# Revit family: Lighting_Outside_Focus-Lighting_Nyx-330_Lantern
name_source: partatom
category: Lighting Fixtures
revit_build: Autodesk Revit 2017 (Build: 20181011_1645(x64)
units: mm (PartAtom-declared; Revit-internal decimal feet)

## family parameters
Always vertical = Yes
Cut with Voids When Loaded = No
Light Source = Yes
OmniClass Number = 23.80.70.14
OmniClass Title = Luminaries for External Lighting
Part Type = Normal
Room Calculation Point = No
Round Connector Dimension = Use Diameter
Shared = No
Work Plane-Based = No

## types (1)
- NYX 330 Lantern
    ArticleNumber = 8914-
    AssetType = Fixed
    BIMObjectName = Lighting_Outside_Focus-Lighting_Nyx-330_Lantern
    Brand = Focus Lighting
    Category = Outdoor
    Collection = Nyx 330
    Color = Various
    Color Filter = 16777215
    ColourRenderingIndex = min 70 Ra, typically 75 Ra, 80 Ra optional
    ColourTolerance = 4 Steps SDCM
    ConvergoRefNr = 0147-1907-0001-DK
    CorrosionResistance = C4
    DefaultElevation = 0 mm  [stored 0 ft]
    Description = The Nyx 330 lantern is suitable for 3 to 6 meter poles. The lantern will fit any pole type with a top diameter of 60 mm.
    Designer = Vilhelm Lauritzen Architects
    Dimming = Programming range 15-100%
DALI (4-conductor), Line switch, AmpDim
    Dimming Lamp Color Temperature Shift = <None>
    Driver = Xitanium Full Xi FP 40 W 0.2-0.7 A
    DurationUnit = Hours
    ElectricalDeviceNominalPower = 0
    ExpectedLife = min 120,000 hours at ta max 25°, L80B10
    Features = Mounting: On pole w. 60 mm top diameter; Adapter for 48 and 42 mm poles; Available with penetrated housing for multiple lanterns on Ø60mm poles. Connection: In the pole; The luminaire is supplied with 5.5 m lead 2x1 mm2
    Finish = Cast aluminium : Graphite grey: SW302G (close to RAL 9007); Silver grey: MW300D; Black: Noir 900 Sablé, SN351F or RAL 9005; Corten brown: Mars YX355F. Diffuser: Polycarbonate, clear.
    HasProtectiveEarth = No
    IP_Code = IP 66
    IfcExportAs = IfcLightFixtureType
    IfcExportType = NOTDEFINED
    ImpactResistance = IK10
    IntensityClass = G*3
    LensMaterial = Clear polycarbonate
    LightFixtureMountingType = Surface
    LightFixturePlacingType = Floor
    LightSource = FF-DA, T3, for local roads, P, HS, and C classes
    LightingProtectionClassification = Class II
    MaintenanceFactor = 0
    Manufacturer = Focus Lighting
    ManufacturerName = Focus Lighting
    ManufacturerURL = https://www.focus-lighting.dk
    Material = Cast aluminium & polycarbonate
    Model = NYX 330 Lantern
    ModelReference = 8914-
    NBSDescription = General purpose luminaires
    NBSReference = 90-60-50/405
    Name = Nyx-330_Lantern
    NominalCurrent = 0 A
    NominalDepth = 440 mm  [stored 1.44357 ft]
    NominalFrequencyRange = 50 Hz
    NominalHeight = 5200 mm  [stored 17.0604 ft]
    NominalVoltage = 220 V
    NominalVoltageCalc = 220 V
    NominalWidth = 330 mm
    NumberOfPoles = 1
    NumberOfSources = 0
    OtherControlOptions = DALI, Line switch, AmpDim; DALI via Zhaga book 18 socket
    OutputRatio = 87.5%
    PhaseAngle = 0.00°
    Photometric Web File = Nyx 330_FFg4DA_T3_730.IES
    ProductDatasheet = https://www.focus-lighting.dk
    ProductInformation = The Nyx 330 lantern is suitable for 3 to 6 meter poles. The lantern will fit any pole type with a top diameter of 60 mm.
    Shape = Sculptured
    Size = 330 x 440 x 5200 mm
    Tilt Angle = 90.00°
    TotalWattage = 40 W
    URL = https://www.focus-lighting.dk
    Uniclass2 = Pr_70_70_49_43
    Uniclass2015Description = Light-emitting diode (LED) luminaires
    Uniclass2015Reference = Pr_70_70_48_46
    UsageCurrent = 22 A
    Version = 1
    VersionDate = 01/07/2019
    WarrantyDurationUnit = Hours
    Weight = 8 kg

note: [stored X ft] marks values corroborated as IEEE doubles in the binary element streams (Revit-internal decimal feet)

## geometry (parser evidence)
native form markers: Sweep x2
no freeform markers — native parametric forms only
